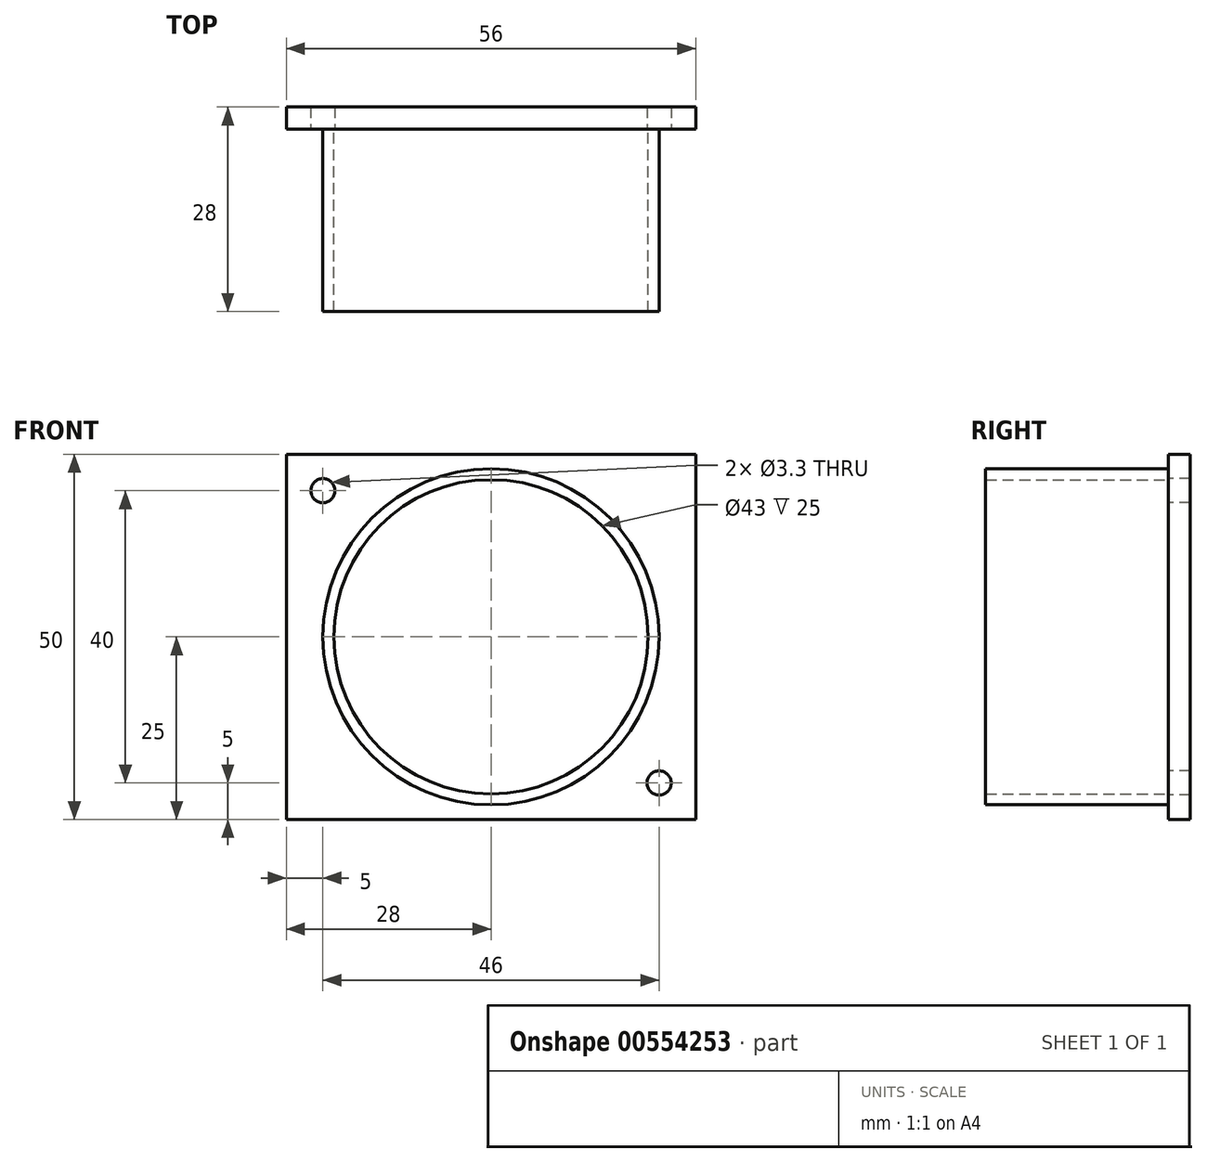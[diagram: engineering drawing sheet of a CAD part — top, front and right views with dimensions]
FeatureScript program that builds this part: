
annotation { "Feature Type Name" : "Feature", "Feature Type Description" : "" }
export const myFeature = defineFeature(function(context is Context, id is Id, definition is map)
    precondition{}
    {
        {
            var Q0;
            Q0=qCreatedBy(makeId("Front.planeOp"),FACE);
            var sketch = newSketch(context, id + "F0", { "sketchPlane" : qUnion([Q0])});
            skCircle(sketch, "E0", {"center": v(0, 0) * mm, "radius": 23 * mm});
            skCircle(sketch, "E1", {"center": v(0, 0) * mm, "radius": 21.5 * mm});
            skLineSegment(sketch, "E2.bottom", {"start": v(28, -25) * mm, "end": v(-28, -25) * mm});
            skLineSegment(sketch, "E2.top", {"start": v(28, 25) * mm, "end": v(-28, 25) * mm});
            skLineSegment(sketch, "E2.left", {"start": v(28, -25) * mm, "end": v(28, 25) * mm});
            skLineSegment(sketch, "E2.right", {"start": v(-28, -25) * mm, "end": v(-28, 25) * mm});
            skPoint(sketch, "E3", {"position": v(-23, 20) * mm});
            skPoint(sketch, "E4", {"position": v(23, -20) * mm});
            skCircle(sketch, "E5", {"center": v(-23, 20) * mm, "radius": 1.65 * mm});
            skCircle(sketch, "E6", {"center": v(23, -20) * mm, "radius": 1.65 * mm});
            skSolve(sketch);
        }
        {
            var Q0;
            Q0=makeQuery(id+"F0.imprint","IMPRINT",FACE,{"disambiguationData":[TD([[makeQuery(id+"F0.imprint","IMPRINT",EDGE,{"derivedFrom":sQuery(id+"F0.wireOp",EDGE,"E0")}),-1.0]])]});
            var Q1;
            Q1=makeQuery(id+"F0.imprint","IMPRINT",FACE,{"disambiguationData":[TD([[makeQuery(id+"F0.imprint","IMPRINT",EDGE,{"derivedFrom":sQuery(id+"F0.wireOp",EDGE,"E1")}),1.0]])]});
            var Q2;
            Q2=makeQuery(id+"F0.imprint","IMPRINT",FACE,{"disambiguationData":[TD([[makeQuery(id+"F0.imprint","IMPRINT",EDGE,{"derivedFrom":sQuery(id+"F0.wireOp",EDGE,"E0")}),1.0]])]});
            var Q3;
            Q3=makeQuery(id+"F0.imprint","IMPRINT",FACE,{"disambiguationData":[TD([[makeQuery(id+"F0.imprint","IMPRINT",EDGE,{"derivedFrom":sQuery(id+"F0.wireOp",EDGE,"E6")}),1.0]])]});
            var Q4;
            Q4=makeQuery(id+"F0.imprint","IMPRINT",FACE,{"disambiguationData":[TD([[makeQuery(id+"F0.imprint","IMPRINT",EDGE,{"derivedFrom":sQuery(id+"F0.wireOp",EDGE,"E5")}),1.0]])]});
            extrude(context, id + "F1", {"entities" : qUnion([Q0, Q1, Q2, Q3, Q4]), "depth" : 28 * mm, "offsetDistance" : 25 * mm});
        }
        {
            var Q0;
            Q0=makeQuery(id+"F1.opExtrude","CAP_FACE",FACE,{"disambiguationData":[OSD([sQuery(id+"F0.wireOp",EDGE,"E2.bottom"),sQuery(id+"F0.wireOp",EDGE,"E2.top"),sQuery(id+"F0.wireOp",EDGE,"E2.left"),sQuery(id+"F0.wireOp",EDGE,"E2.right")])],"isStart":false});
            var sketch = newSketch(context, id + "F2", { "sketchPlane" : qUnion([Q0])});
            skCircle(sketch, "E7", {"center": v(0, 0) * mm, "radius": 21.5 * mm});
            skCircle(sketch, "E8", {"center": v(0, 0) * mm, "radius": 23 * mm});
            skSolve(sketch);
        }
        {
            var Q0;
            Q0=makeQuery(id+"F2.imprint","IMPRINT",FACE,{"disambiguationData":[TD([[makeQuery(id+"F2.imprint","IMPRINT",EDGE,{"derivedFrom":sQuery(id+"F2.wireOp",EDGE,"E7")}),1.0]])]});
            extrude(context, id + "F3", {"entities" : qUnion([Q0]), "operationType" : NewBodyOperationType.REMOVE, "oppositeDirection" : true, "depth" : 25 * mm, "offsetDistance" : 25 * mm});
        }
        {
            var Q0;
            Q0=makeQuery(id+"F1.opExtrude","CAP_FACE",FACE,{"disambiguationData":[OSD([sQuery(id+"F0.wireOp",EDGE,"E2.bottom"),sQuery(id+"F0.wireOp",EDGE,"E2.top"),sQuery(id+"F0.wireOp",EDGE,"E2.left"),sQuery(id+"F0.wireOp",EDGE,"E2.right")])],"isStart":false});
            var sketch = newSketch(context, id + "F4", { "sketchPlane" : qUnion([Q0])});
            skPoint(sketch, "E9", {"position": v(-23, 20) * mm});
            skPoint(sketch, "E10", {"position": v(23, -20) * mm});
            skCircle(sketch, "E11", {"center": v(-23, 20) * mm, "radius": 1.65 * mm});
            skCircle(sketch, "E12", {"center": v(23, -20) * mm, "radius": 1.65 * mm});
            skSolve(sketch);
        }
        {
            var Q0;
            Q0=makeQuery(id+"F4.imprint","IMPRINT",FACE,{"disambiguationData":[TD([[makeQuery(id+"F4.imprint","IMPRINT",EDGE,{"derivedFrom":sQuery(id+"F4.wireOp",EDGE,"E11")}),1.0]])]});
            var Q1;
            Q1=makeQuery(id+"F4.imprint","IMPRINT",FACE,{"disambiguationData":[TD([[makeQuery(id+"F4.imprint","IMPRINT",EDGE,{"derivedFrom":sQuery(id+"F4.wireOp",EDGE,"E12")}),1.0]])]});
            extrude(context, id + "F5", {"entities" : qUnion([Q0, Q1]), "operationType" : NewBodyOperationType.REMOVE, "endBound" : BoundingType.THROUGH_ALL, "oppositeDirection" : true, "depth" : 25 * mm, "offsetDistance" : 25 * mm});
        }
        {
            var Q0;
            Q0=makeQuery(id+"F3.boolean.opBoolean","COPY",FACE,{"derivedFrom":makeQuery(id+"F3.opExtrude","CAP_FACE",FACE,{"disambiguationData":[OSD([sQuery(id+"F2.wireOp",EDGE,"E7")])],"isStart":false})});
            var sketch = newSketch(context, id + "F6", { "sketchPlane" : qUnion([Q0])});
            skCircle(sketch, "E13", {"center": v(0, 0) * mm, "radius": 23 * mm});
            skSolve(sketch);
        }
        {
            var Q0;
            Q0=makeQuery(id+"F1.opExtrude","CAP_FACE",FACE,{"disambiguationData":[OSD([sQuery(id+"F0.wireOp",EDGE,"E2.bottom"),sQuery(id+"F0.wireOp",EDGE,"E2.top"),sQuery(id+"F0.wireOp",EDGE,"E2.left"),sQuery(id+"F0.wireOp",EDGE,"E2.right")])],"isStart":false});
            extrude(context, id + "F7", {"entities" : qUnion([Q0]), "operationType" : NewBodyOperationType.REMOVE, "oppositeDirection" : true, "depth" : 25 * mm, "offsetDistance" : 25 * mm});
        }
        {
            var Q0;
            Q0=makeQuery(id+"F6.imprint","IMPRINT",FACE,{"disambiguationData":[TD([[makeQuery(id+"F6.imprint","IMPRINT",EDGE,{"derivedFrom":sQuery(id+"F6.wireOp",EDGE,"E13")}),1.0]])]});
            extrude(context, id + "F8", {"entities" : qUnion([Q0]), "operationType" : NewBodyOperationType.ADD, "depth" : 25 * mm, "offsetDistance" : 25 * mm});
        }
    });
